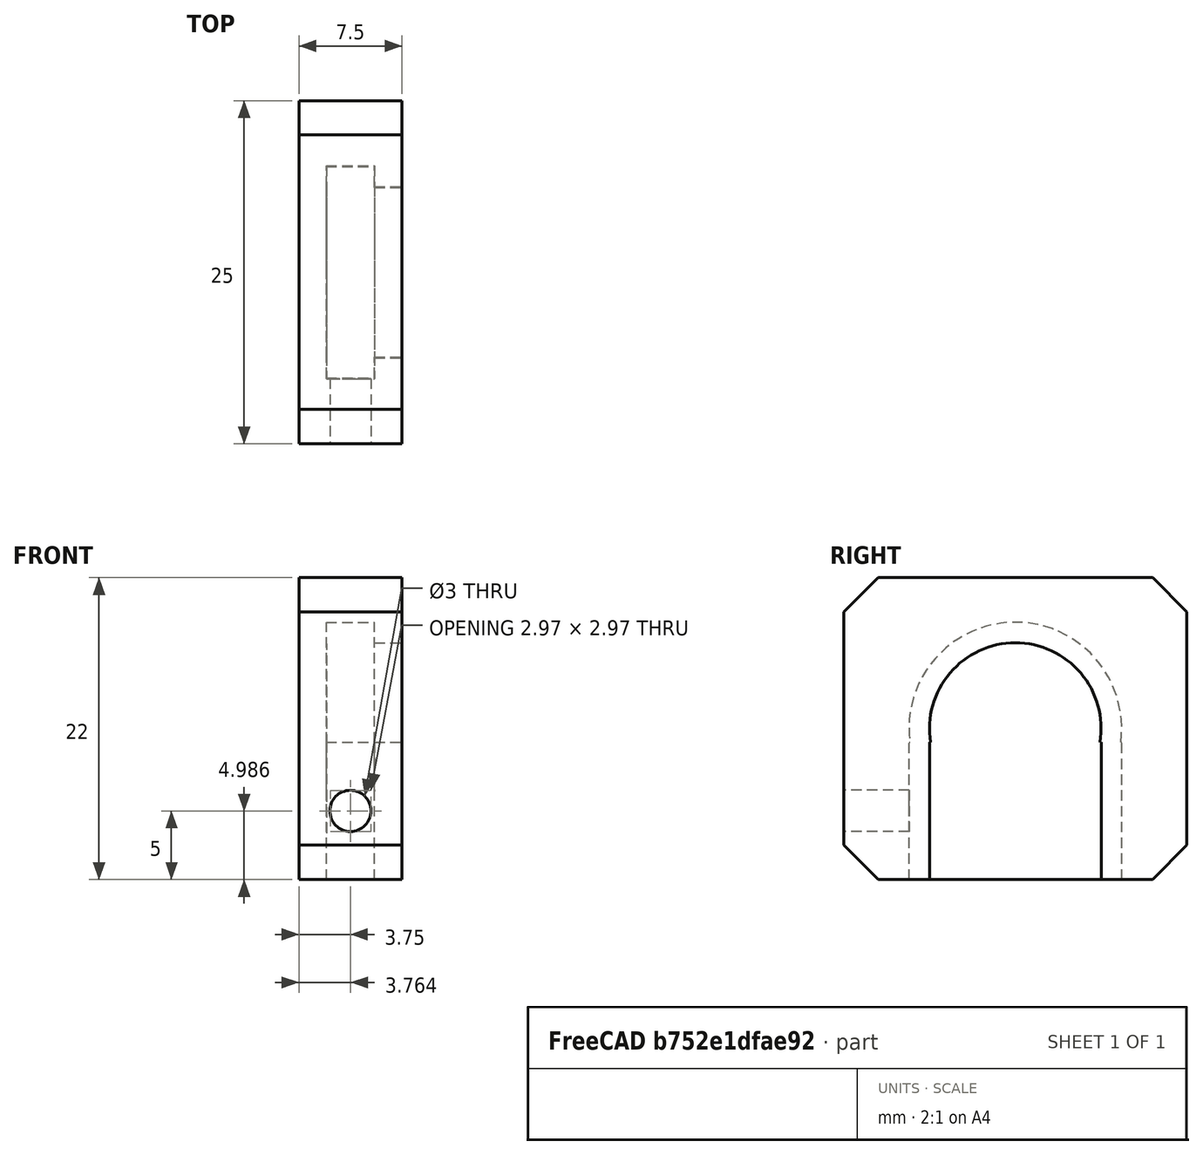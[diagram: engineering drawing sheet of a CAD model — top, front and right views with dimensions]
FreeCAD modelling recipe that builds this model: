
FCSTD DOCUMENT
Label: PhoneSocket
objects: Part::Cut×5, Part::Box×3, Part::Cylinder×3, Part::Chamfer×2
note: 13 computed .brp shape members not serialized (recipe doc carries the construction recipe); baked Part::Feature solids carry a one-line shape summary decoded from their .brp

FEATURE [Part::Box] Box
  Height = 22
  Length = 7.5
  Width = 25
FEATURE [Part::Cylinder] Cylinder
  Angle = 360
  Height = 10
  Placement = pos=(2,12.5,11) rot=(0,1,0;1.5708rad)
  Radius = 6.25
FEATURE [Part::Cut] Cut
  Base = -> Box
  Tool = -> Cylinder
FEATURE [Part::Cylinder] Cylinder001
  Angle = 360
  Height = 3.5
  Radius = 7.75
FEATURE [Part::Cut] Cut001
  Base = -> Cut
  Tool = -> Cylinder001
FEATURE [Part::Box] Box001
  Height = 10
  Length = 3.5
  Placement = pos=(2,4.75,0) rot=(0,0,1;0rad)
  Width = 15.5
FEATURE [Part::Cut] Cut002
  Base = -> Cut001
  Tool = -> Box001
FEATURE [Part::Box] Box002
  Height = 10
  Length = 7
  Placement = pos=(2,6.25,0) rot=(0,0,1;0rad)
  Width = 12.5
FEATURE [Part::Cut] Cut003
  Base = -> Cut002
  Tool = -> Box002
FEATURE [Part::Chamfer] Chamfer
  Base = -> Cut003
  Edges = 2 edges r=2.5: [Edge7,Edge8]
FEATURE [Part::Chamfer] Chamfer001
  Base = -> Chamfer
  Edges = 2 edges r=2.5: [Edge9,Edge16]
FEATURE [Part::Cylinder] Cylinder002
  Angle = 360
  Height = 7
  Placement = pos=(3.75,6,5) rot=(1,0,0;1.5708rad)
  Radius = 1.5
FEATURE [Part::Cut] Cut004
  Base = -> Chamfer001
  Tool = -> Cylinder002
